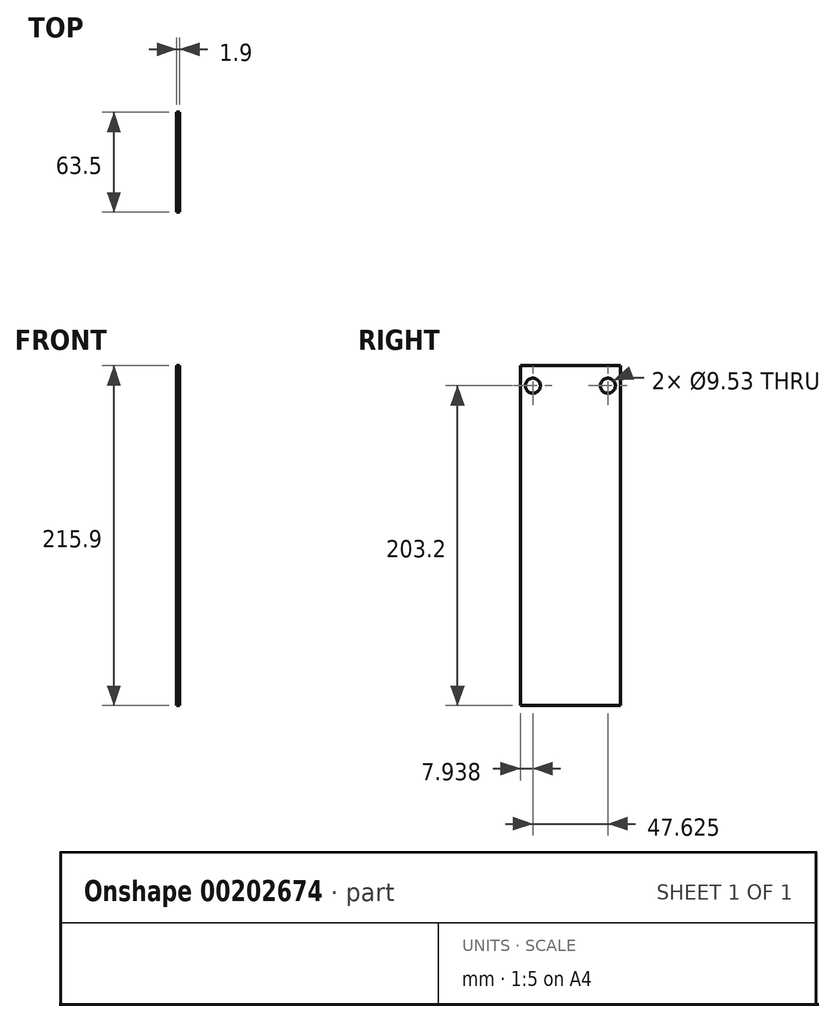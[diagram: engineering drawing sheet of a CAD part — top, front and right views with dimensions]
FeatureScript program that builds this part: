
annotation { "Feature Type Name" : "Feature", "Feature Type Description" : "" }
export const myFeature = defineFeature(function(context is Context, id is Id, definition is map)
    precondition{}
    {
        {
            var Q0;
            Q0=qCreatedBy(makeId("Right.planeOp"),FACE);
            var sketch = newSketch(context, id + "F0", { "sketchPlane" : qUnion([Q0])});
            skLineSegment(sketch, "E0.bottom", {"start": v(31.75, 107.95) * mm, "end": v(-31.75, 107.95) * mm});
            skLineSegment(sketch, "E0.top", {"start": v(31.75, -107.95) * mm, "end": v(-31.75, -107.95) * mm});
            skLineSegment(sketch, "E0.left", {"start": v(31.75, 107.95) * mm, "end": v(31.75, -107.95) * mm});
            skLineSegment(sketch, "E0.right", {"start": v(-31.75, 107.95) * mm, "end": v(-31.75, -107.95) * mm});
            skPoint(sketch, "E0.middle", {"position": v(0, 0) * mm});
            skSolve(sketch);
        }
        {
            var Q0;
            Q0 = qSketchRegion(id + "F0", true);
            extrude(context, id + "F1", {"entities" : qUnion([Q0]), "depth" : 1.9 * mm});
        }
        {
            var Q0;
            Q0=makeQuery(id+"F1.opExtrude","CAP_FACE",FACE,{"disambiguationData":[OSD([sQuery(id+"F0.wireOp",EDGE,"E0.bottom"),sQuery(id+"F0.wireOp",EDGE,"E0.top"),sQuery(id+"F0.wireOp",EDGE,"E0.left"),sQuery(id+"F0.wireOp",EDGE,"E0.right")])],"isStart":true});
            var sketch = newSketch(context, id + "F2", { "sketchPlane" : qUnion([Q0])});
            skCircle(sketch, "E1", {"center": v(-23.81, 95.25) * mm, "radius": 4.76 * mm});
            skCircle(sketch, "E2", {"center": v(23.81, 95.25) * mm, "radius": 4.76 * mm});
            skSolve(sketch);
        }
        {
            var Q0;
            Q0 = qSketchRegion(id + "F2", true);
            extrude(context, id + "F3", {"entities" : qUnion([Q0]), "operationType" : NewBodyOperationType.REMOVE, "oppositeDirection" : true, "depth" : 25.4 * mm});
        }
    });
